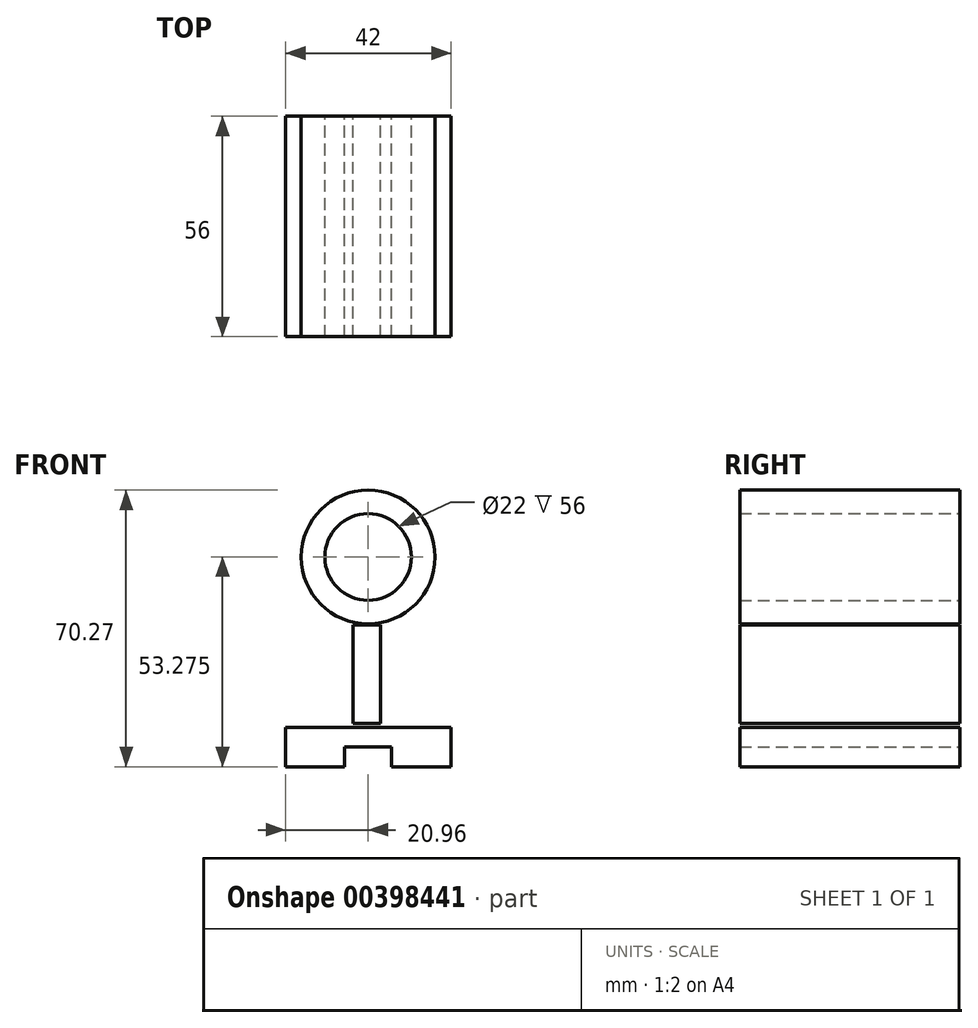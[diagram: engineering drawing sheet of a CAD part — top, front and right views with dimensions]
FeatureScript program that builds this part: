
annotation { "Feature Type Name" : "Feature", "Feature Type Description" : "" }
export const myFeature = defineFeature(function(context is Context, id is Id, definition is map)
    precondition{}
    {
        {
            var Q0;
            Q0=qCreatedBy(makeId("Front.planeOp"),FACE);
            var sketch = newSketch(context, id + "F0", { "sketchPlane" : qUnion([Q0])});
            skCircle(sketch, "E0", {"center": v(0, 39.37) * mm, "radius": 17 * mm});
            skCircle(sketch, "E1", {"center": v(0, 39.37) * mm, "radius": 11 * mm});
            skSolve(sketch);
        }
        {
            var Q0;
            Q0=qCreatedBy(makeId("Front.planeOp"),FACE);
            var sketch = newSketch(context, id + "F1", { "sketchPlane" : qUnion([Q0])});
            skLineSegment(sketch, "E2.bottom", {"start": v(3.2, -2.9) * mm, "end": v(-3.8, -2.9) * mm});
            skLineSegment(sketch, "E2.top", {"start": v(3.2, 22.1) * mm, "end": v(-3.8, 22.1) * mm});
            skLineSegment(sketch, "E2.left", {"start": v(3.2, -2.9) * mm, "end": v(3.2, 22.1) * mm});
            skLineSegment(sketch, "E2.right", {"start": v(-3.8, -2.9) * mm, "end": v(-3.8, 22.1) * mm});
            skPoint(sketch, "E2.middle", {"position": v(-0.3, 9.6) * mm});
            skLineSegment(sketch, "E3.bottom", {"start": v(21.04, -13.9) * mm, "end": v(-20.96, -13.9) * mm});
            skLineSegment(sketch, "E3.top", {"start": v(21.04, -3.9) * mm, "end": v(-20.96, -3.9) * mm});
            skLineSegment(sketch, "E3.left", {"start": v(21.04, -13.9) * mm, "end": v(21.04, -3.9) * mm});
            skLineSegment(sketch, "E3.right", {"start": v(-20.96, -13.9) * mm, "end": v(-20.96, -3.9) * mm});
            skPoint(sketch, "E3.middle", {"position": v(0.04, -8.9) * mm});
            skLineSegment(sketch, "E4.bottom", {"start": v(6, -13.9) * mm, "end": v(-6, -13.9) * mm});
            skLineSegment(sketch, "E4.top", {"start": v(6, -8.9) * mm, "end": v(-6, -8.9) * mm});
            skLineSegment(sketch, "E4.left", {"start": v(6, -13.9) * mm, "end": v(6, -8.9) * mm});
            skLineSegment(sketch, "E4.right", {"start": v(-6, -13.9) * mm, "end": v(-6, -8.9) * mm});
            skPoint(sketch, "E4.middle", {"position": v(0, -11.4) * mm});
            skSolve(sketch);
        }
        {
            var Q0;
            Q0=makeQuery(id+"F1.imprint","IMPRINT",FACE,{"disambiguationData":[TD([[makeQuery(id+"F1.imprint","IMPRINT",EDGE,{"derivedFrom":sQuery(id+"F1.wireOp",EDGE,"E2.bottom")}),-1.0]])]});
            var Q1;
            Q1=makeQuery(id+"F0.imprint","IMPRINT",FACE,{"disambiguationData":[TD([[makeQuery(id+"F0.imprint","IMPRINT",EDGE,{"derivedFrom":sQuery(id+"F0.wireOp",EDGE,"E0")}),1.0]])]});
            var Q2;
            Q2=makeQuery(id+"F1.imprint","IMPRINT",FACE,{"disambiguationData":[TD([[makeQuery(id+"F1.imprint","IMPRINT",EDGE,{"derivedFrom":sQuery(id+"F1.wireOp",EDGE,"E3.top")}),1.0]])]});
            extrude(context, id + "F2", {"entities" : qUnion([Q0, Q1, Q2]), "depth" : 56 * mm});
        }
    });
